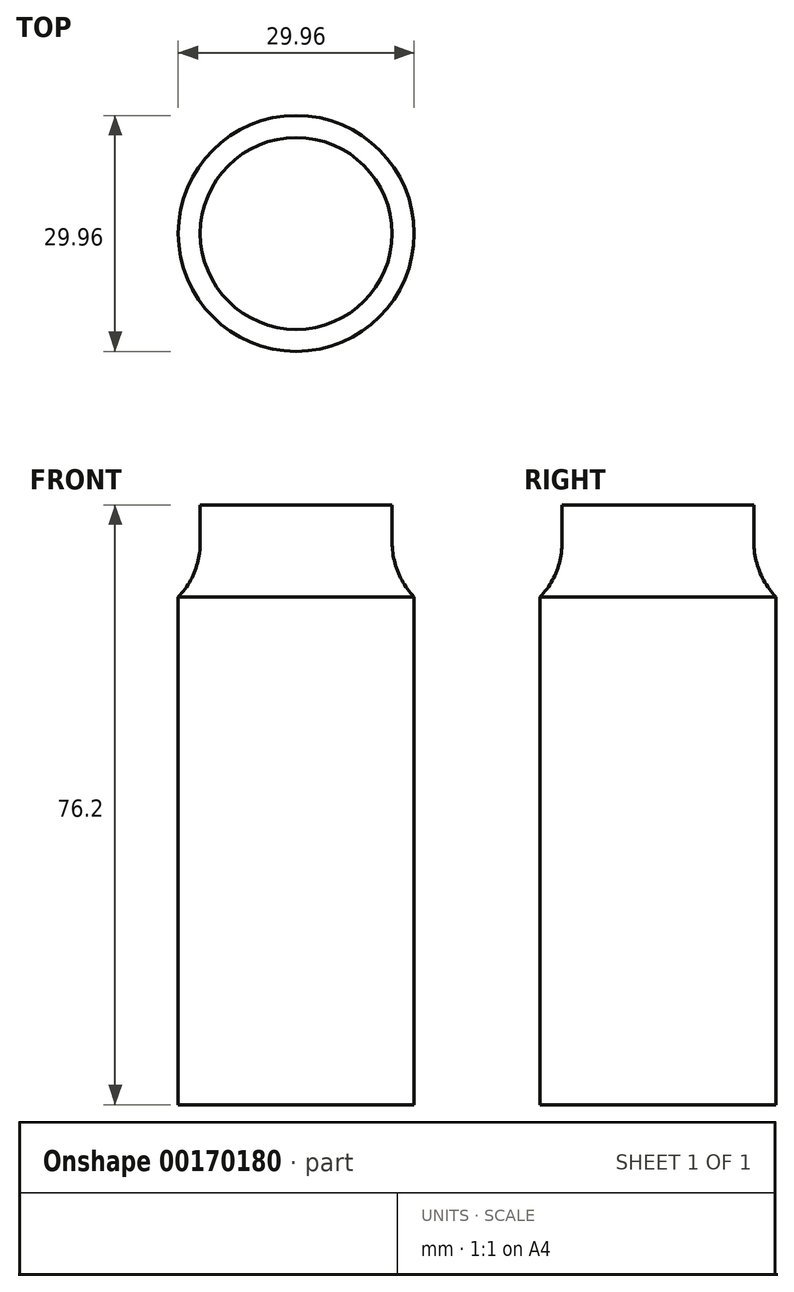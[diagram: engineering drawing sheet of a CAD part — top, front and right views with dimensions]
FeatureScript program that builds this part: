
annotation { "Feature Type Name" : "Feature", "Feature Type Description" : "" }
export const myFeature = defineFeature(function(context is Context, id is Id, definition is map)
    precondition{}
    {
        {
            var Q0;
            Q0=qCreatedBy(makeId("Top.planeOp"),FACE);
            var sketch = newSketch(context, id + "F0", { "sketchPlane" : qUnion([Q0])});
            skLineSegment(sketch, "E0.bottom", {"start": v(25.4, 25.4) * mm, "end": v(-25.4, 25.4) * mm});
            skLineSegment(sketch, "E0.top", {"start": v(25.4, -25.4) * mm, "end": v(-25.4, -25.4) * mm});
            skLineSegment(sketch, "E0.left", {"start": v(25.4, 25.4) * mm, "end": v(25.4, -25.4) * mm});
            skLineSegment(sketch, "E0.right", {"start": v(-25.4, 25.4) * mm, "end": v(-25.4, -25.4) * mm});
            skPoint(sketch, "E0.middle", {"position": v(0, 0) * mm});
            skCircle(sketch, "E1", {"center": v(0, 0) * mm, "radius": 12.7 * mm});
            skSolve(sketch);
        }
        {
            var Q0;
            Q0=qCreatedBy(makeId("Front.planeOp"),FACE);
            var sketch = newSketch(context, id + "F1", { "sketchPlane" : qUnion([Q0])});
            skLineSegment(sketch, "E2.bottom", {"start": v(0, 4.76) * mm, "end": v(-13.97, 4.76) * mm});
            skLineSegment(sketch, "E2.top", {"start": v(0, -4.76) * mm, "end": v(-13.97, -4.76) * mm});
            skLineSegment(sketch, "E2.left", {"start": v(0, 4.76) * mm, "end": v(0, -4.76) * mm});
            skLineSegment(sketch, "E2.right", {"start": v(-13.97, 4.76) * mm, "end": v(-13.97, -4.76) * mm});
            skLineSegment(sketch, "E3", {"start": v(-12.7, 4.76) * mm, "end": v(-12.7, -4.76) * mm, "construction": true});
            skArc(sketch, "E4", {"start": v(-13.97, -4.76) * mm, "mid": v(-12.7, 0) * mm, "end": v(-13.97, 4.76) * mm});
            skLineSegment(sketch, "E5", {"start": v(-12.7, 0) * mm, "end": v(-13.97, 0) * mm});
            skLineSegment(sketch, "E6", {"start": v(-13.97, 4.76) * mm, "end": v(-37.02, 4.76) * mm});
            skLineSegment(sketch, "E7", {"start": v(-37.02, 4.76) * mm, "end": v(-37.02, -4.76) * mm});
            skLineSegment(sketch, "E8", {"start": v(-37.02, -4.76) * mm, "end": v(-13.97, -4.76) * mm});
            skSolve(sketch);
        }
        {
            var Q0;
            Q0=qCreatedBy(makeId("Front.planeOp"),FACE);
            var sketch = newSketch(context, id + "F2", { "sketchPlane" : qUnion([Q0])});
            skLineSegment(sketch, "E9.0", {"start": v(0, 4.76) * mm, "end": v(-12.19, 4.76) * mm});
            skPoint(sketch, "E10.third.point", {"position": v(-12.73, -0.86) * mm});
            skArc(sketch, "E11.0", {"start": v(-14.98, -6.95) * mm, "mid": v(-12.91, -3.75) * mm, "end": v(-12.19, 0) * mm});
            skLineSegment(sketch, "E12", {"start": v(-14.98, -6.95) * mm, "end": v(-14.98, -71.44) * mm});
            skLineSegment(sketch, "E13", {"start": v(-14.98, -71.44) * mm, "end": v(0, -71.44) * mm});
            skLineSegment(sketch, "E14", {"start": v(0, -71.44) * mm, "end": v(0, 4.76) * mm});
            skLineSegment(sketch, "E15", {"start": v(-12.19, 0) * mm, "end": v(-12.19, 4.76) * mm});
            skPoint(sketch, "E15.startSnap0", {"position": v(-13.97, 0) * mm});
            skLineSegment(sketch, "E16", {"start": v(-12.19, 4.76) * mm, "end": v(0, 4.76) * mm});
            skPoint(sketch, "E17.orphan", {"position": v(0, -4.76) * mm});
            skPoint(sketch, "E18.trimOffspring.end.orphan", {"position": v(-13.97, 4.76) * mm});
            skPoint(sketch, "E19.0.end.orphan", {"position": v(-13.97, -4.76) * mm});
            skSolve(sketch);
        }
        {
            var Q0;
            Q0=makeQuery(id+"F2.imprint","IMPRINT",FACE,{"disambiguationData":[TD([[makeQuery(id+"F2.imprint","IMPRINT",EDGE,{"derivedFrom":sQuery(id+"F2.wireOp",EDGE,"E11.0")}),-1.0]])]});
            var Q1;
            Q1=sQuery(id+"F2.wireOp",EDGE,"E14");
            revolve(context, id + "F3", {"entities" : qUnion([Q0]), "axis" : qUnion([Q1]), "revolveType" : RevolveType.FULL});
        }
    });
